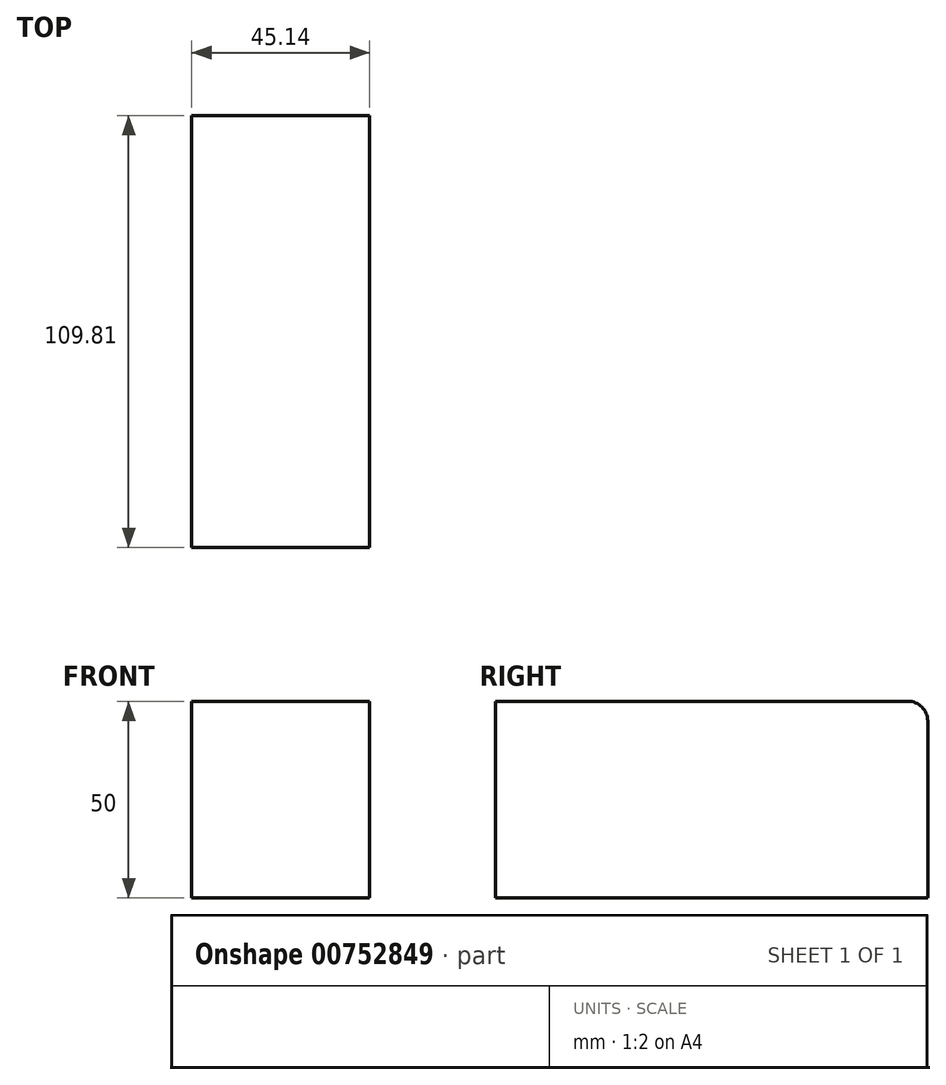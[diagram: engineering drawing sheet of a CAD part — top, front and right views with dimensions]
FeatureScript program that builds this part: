
annotation { "Feature Type Name" : "Feature", "Feature Type Description" : "" }
export const myFeature = defineFeature(function(context is Context, id is Id, definition is map)
    precondition{}
    {
        {
            var Q0;
            Q0=qCreatedBy(makeId("Top.planeOp"),FACE);
            var sketch = newSketch(context, id + "F0", { "sketchPlane" : qUnion([Q0])});
            skLineSegment(sketch, "E0.bottom", {"start": v(-133.2, 26.54) * mm, "end": v(-88.06, 26.54) * mm});
            skLineSegment(sketch, "E0.top", {"start": v(-133.2, -83.27) * mm, "end": v(-88.06, -83.27) * mm});
            skLineSegment(sketch, "E0.left", {"start": v(-133.2, 26.54) * mm, "end": v(-133.2, -83.27) * mm});
            skLineSegment(sketch, "E0.right", {"start": v(-88.06, 26.54) * mm, "end": v(-88.06, -83.27) * mm});
            skSolve(sketch);
        }
        {
            var Q0;
            Q0=makeQuery(id+"F0.imprint","IMPRINT",FACE,{"disambiguationData":[TD([[makeQuery(id+"F0.imprint","IMPRINT",EDGE,{"derivedFrom":sQuery(id+"F0.wireOp",EDGE,"E0.bottom")}),-1.0]])]});
            extrude(context, id + "F1", {"entities" : qUnion([Q0]), "depth" : 50 * mm, "offsetDistance" : 25.4 * mm});
        }
        {
            var Q0;
            Q0=makeQuery(id+"F1.opExtrude","CAP_EDGE",EDGE,{"disambiguationData":[OSD([sQuery(id+"F0.wireOp",EDGE,"E0.bottom")])],"isStart":false});
            fillet(context, id + "F2", {"entities" : qUnion([Q0]), "radius" : 5 * mm, "tangentPropagation" : true, "allowEdgeOverflow" : false});
        }
    });
